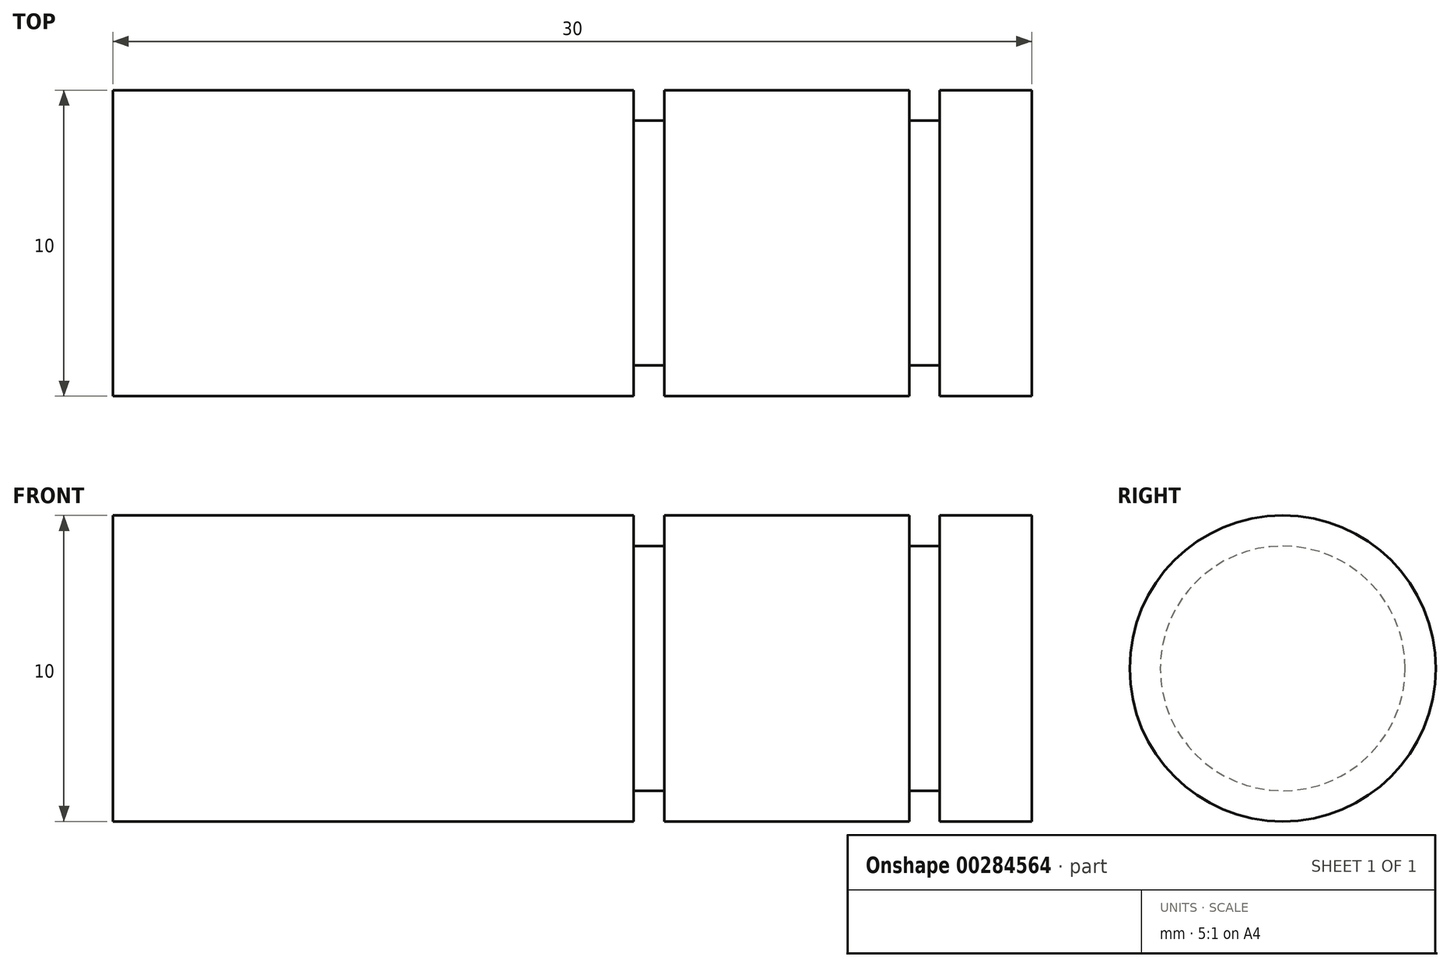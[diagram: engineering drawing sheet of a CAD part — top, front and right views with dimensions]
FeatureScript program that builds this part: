
annotation { "Feature Type Name" : "Feature", "Feature Type Description" : "" }
export const myFeature = defineFeature(function(context is Context, id is Id, definition is map)
    precondition{}
    {
        {
            var Q0;
            Q0=qCreatedBy(makeId("Front.planeOp"),FACE);
            var sketch = newSketch(context, id + "F0", { "sketchPlane" : qUnion([Q0])});
            skLineSegment(sketch, "E0", {"start": v(0, 0) * mm, "end": v(0, 5) * mm});
            skLineSegment(sketch, "E1", {"start": v(0, 5) * mm, "end": v(17, 5) * mm});
            skLineSegment(sketch, "E2", {"start": v(30, 5) * mm, "end": v(30, 0) * mm});
            skLineSegment(sketch, "E3", {"start": v(30, 0) * mm, "end": v(0, 0) * mm});
            skLineSegment(sketch, "E4.top", {"start": v(17, 4) * mm, "end": v(18, 4) * mm});
            skLineSegment(sketch, "E4.left", {"start": v(17, 5) * mm, "end": v(17, 4) * mm});
            skLineSegment(sketch, "E4.right", {"start": v(18, 5) * mm, "end": v(18, 4) * mm});
            skLineSegment(sketch, "E5.top", {"start": v(26, 4) * mm, "end": v(27, 4) * mm});
            skLineSegment(sketch, "E5.left", {"start": v(26, 5) * mm, "end": v(26, 4) * mm});
            skLineSegment(sketch, "E5.right", {"start": v(27, 5) * mm, "end": v(27, 4) * mm});
            skLineSegment(sketch, "E6.trimOffspring", {"start": v(18, 5) * mm, "end": v(26, 5) * mm});
            skLineSegment(sketch, "E7.trimOffspring", {"start": v(27, 5) * mm, "end": v(30, 5) * mm});
            skLineSegment(sketch, "E8", {"start": v(-15.37, 0) * mm, "end": v(44.9, 0) * mm, "construction": true});
            skSolve(sketch);
        }
        {
            var Q0;
            Q0 = qSketchRegion(id + "F0", true);
            var Q1;
            Q1=sQuery(id+"F0.wireOp",EDGE,"E8");
            revolve(context, id + "F1", {"entities" : qUnion([Q0]), "axis" : qUnion([Q1]), "revolveType" : RevolveType.FULL});
        }
    });
